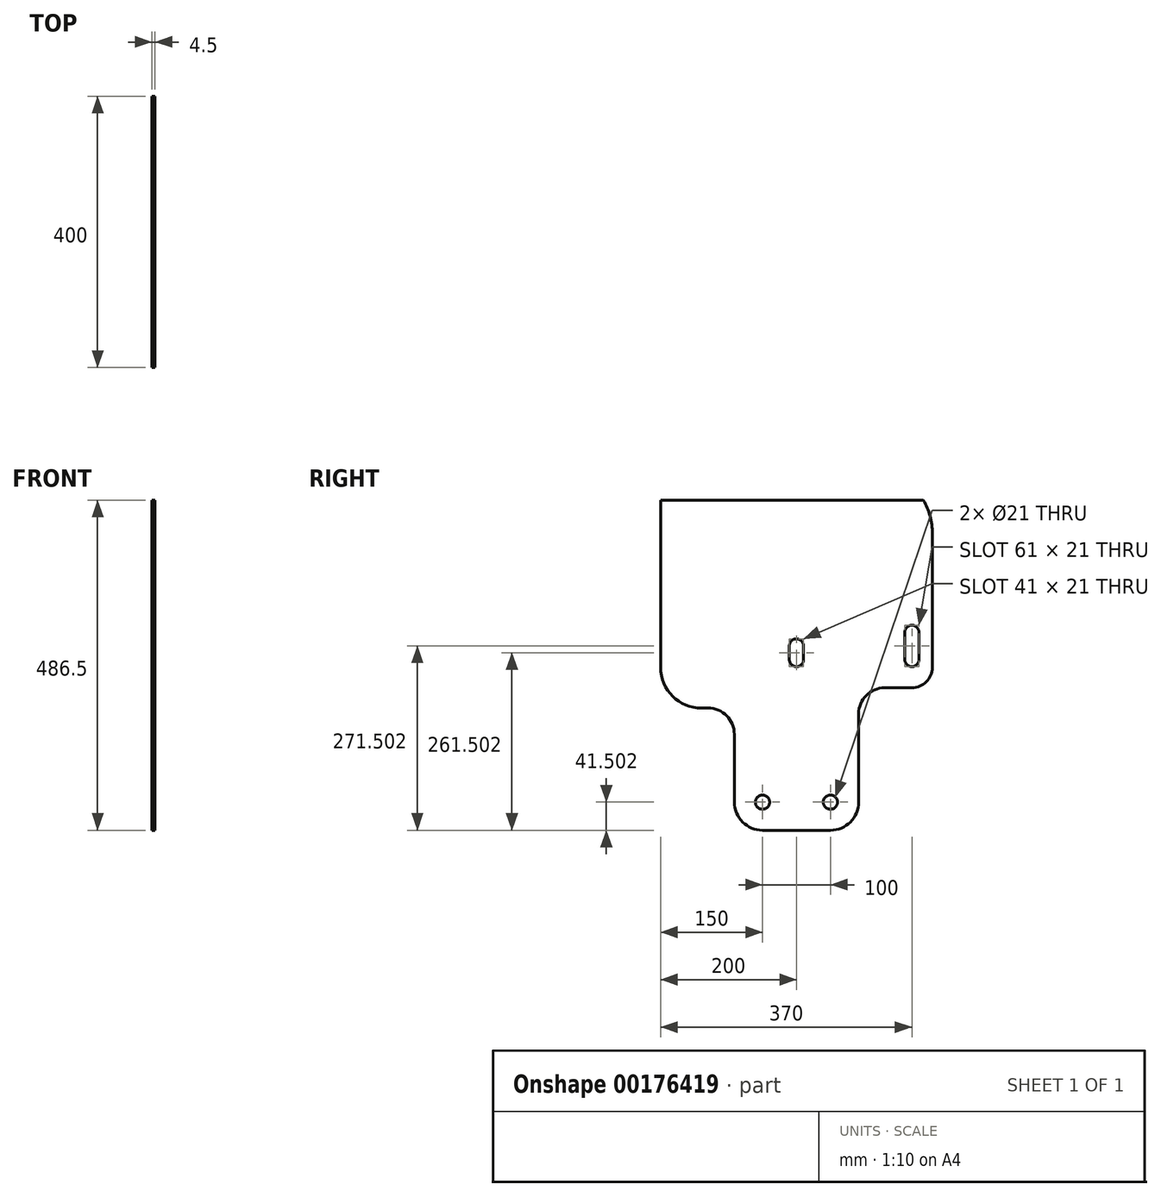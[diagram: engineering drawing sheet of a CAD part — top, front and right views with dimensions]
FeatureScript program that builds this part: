
annotation { "Feature Type Name" : "Feature", "Feature Type Description" : "" }
export const myFeature = defineFeature(function(context is Context, id is Id, definition is map)
    precondition{}
    {
        {
            var Q0;
            Q0=qCreatedBy(makeId("Right.planeOp"),FACE);
            var sketch = newSketch(context, id + "F0", { "sketchPlane" : qUnion([Q0])});
            skLineSegment(sketch, "E0", {"start": v(-100, 303.86) * mm, "end": v(287.06, 303.86) * mm});
            skLineSegment(sketch, "E1", {"start": v(103.65, -11.14) * mm, "end": v(103.66, -11.14) * mm});
            skLineSegment(sketch, "E2", {"start": v(-100, 57.36) * mm, "end": v(-100, 303.86) * mm});
            skLineSegment(sketch, "E3", {"start": v(300, 254.66) * mm, "end": v(300, 57.36) * mm});
            skArc(sketch, "E4", {"start": v(150, -182.64) * mm, "mid": v(179.34, -170.48) * mm, "end": v(191.5, -141.14) * mm});
            skArc(sketch, "E5", {"start": v(8.5, -141.14) * mm, "mid": v(20.66, -170.48) * mm, "end": v(50, -182.64) * mm});
            skArc(sketch, "E6", {"start": v(230, 27.36) * mm, "mid": v(202.78, 16.09) * mm, "end": v(191.5, -11.14) * mm});
            skArc(sketch, "E7", {"start": v(8.5, -41.14) * mm, "mid": v(-2.78, -13.91) * mm, "end": v(-30, -2.64) * mm});
            skLineSegment(sketch, "E8", {"start": v(8.5, -141.14) * mm, "end": v(8.5, -41.14) * mm});
            skLineSegment(sketch, "E9", {"start": v(50, -182.64) * mm, "end": v(150, -182.64) * mm});
            skLineSegment(sketch, "E10", {"start": v(191.5, -141.14) * mm, "end": v(191.5, -11.14) * mm});
            skLineSegment(sketch, "E11", {"start": v(-30, -2.64) * mm, "end": v(-40, -2.64) * mm});
            skLineSegment(sketch, "E12", {"start": v(230, 27.36) * mm, "end": v(270, 27.36) * mm});
            skCircle(sketch, "E13", {"center": v(150, -141.14) * mm, "radius": 10.5 * mm});
            skPoint(sketch, "E14.visualSharp", {"position": v(-100, -2.64) * mm});
            skArc(sketch, "E14.filletArc", {"start": v(-100, 57.36) * mm, "mid": v(-82.43, 14.94) * mm, "end": v(-40, -2.64) * mm});
            skPoint(sketch, "E15.visualSharp", {"position": v(300, 27.36) * mm});
            skCircle(sketch, "E16", {"center": v(50, -141.14) * mm, "radius": 10.5 * mm});
            skPoint(sketch, "E17.visualSharp", {"position": v(-100, -182.64) * mm});
            skPoint(sketch, "E18.visualSharp", {"position": v(300, -182.64) * mm});
            skArc(sketch, "E19", {"start": v(110.5, 88.86) * mm, "mid": v(100, 99.36) * mm, "end": v(89.5, 88.86) * mm});
            skLineSegment(sketch, "E20", {"start": v(100, 88.86) * mm, "end": v(270, 88.86) * mm});
            skArc(sketch, "E21", {"start": v(280.5, 108.86) * mm, "mid": v(270, 119.36) * mm, "end": v(259.5, 108.86) * mm});
            skArc(sketch, "E22", {"start": v(259.5, 68.86) * mm, "mid": v(270, 58.36) * mm, "end": v(280.5, 68.86) * mm});
            skArc(sketch, "E23", {"start": v(89.5, 68.86) * mm, "mid": v(100, 58.36) * mm, "end": v(110.5, 68.86) * mm});
            skLineSegment(sketch, "E24", {"start": v(259.5, 108.86) * mm, "end": v(259.5, 68.86) * mm});
            skLineSegment(sketch, "E25", {"start": v(280.5, 108.86) * mm, "end": v(280.5, 68.86) * mm});
            skLineSegment(sketch, "E26", {"start": v(110.5, 68.86) * mm, "end": v(110.5, 88.86) * mm});
            skLineSegment(sketch, "E27", {"start": v(89.5, 68.86) * mm, "end": v(89.5, 88.86) * mm});
            skPoint(sketch, "E28.orphan", {"position": v(-100, 303.86) * mm});
            skPoint(sketch, "E29.orphan", {"position": v(300, 303.86) * mm});
            skArc(sketch, "E30", {"start": v(300, 254.66) * mm, "mid": v(296.71, 280.1) * mm, "end": v(287.06, 303.86) * mm});
            skArc(sketch, "E31.filletArc", {"start": v(270, 27.36) * mm, "mid": v(291.21, 36.15) * mm, "end": v(300, 57.36) * mm});
            skSolve(sketch);
        }
        {
            var Q0;
            {var subQ5=sQuery(id+"F0.wireOp",EDGE,"E2");Q0=makeQuery(id+"F0.imprint","IMPRINT",FACE,{"disambiguationData":[TD([[makeQuery(id+"F0.imprint","IMPRINT",EDGE,{"derivedFrom":subQ5}),-1.0]])]});}
            extrude(context, id + "F1", {"entities" : qUnion([Q0]), "depth" : 4.5 * mm});
        }
    });
